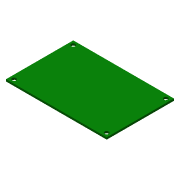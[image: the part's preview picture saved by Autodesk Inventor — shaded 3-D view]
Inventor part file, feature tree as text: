
AUTODESK INVENTOR PART (.ipt)
format: ipt  version: 2015 (Build 190159000, 159)  size: 89,088 bytes
history: native  units: in
note: dims shown in document units (in); Inventor stores cm internally (conversion verified against a paired STEP export)
features: extrude x2, sketch x2
ambient origin geometry x8: Origin, YZ Plane, XZ Plane, XY Plane, X Axis, Y Axis, Z Axis, Center Point
bodies: Solid1 (feature_tree)
feature tree (4):
  extrude  "Extrusion1"  Depth=2.01in
  extrude  "Extrusion2"  Depth=0.06in
  sketch  "Sketch1"  dims[d0=3.01in d1=2.01in]
  sketch  "Sketch2"  dims[d2=0.06in d3=0.0in d4=0.125in d5=0.12in d6=0.12in d7=0.12in d8=0.12in d9=0.12in d10=0.12in d11=0.12in d12=0.12in d13=1.0in d14=0.0in]
